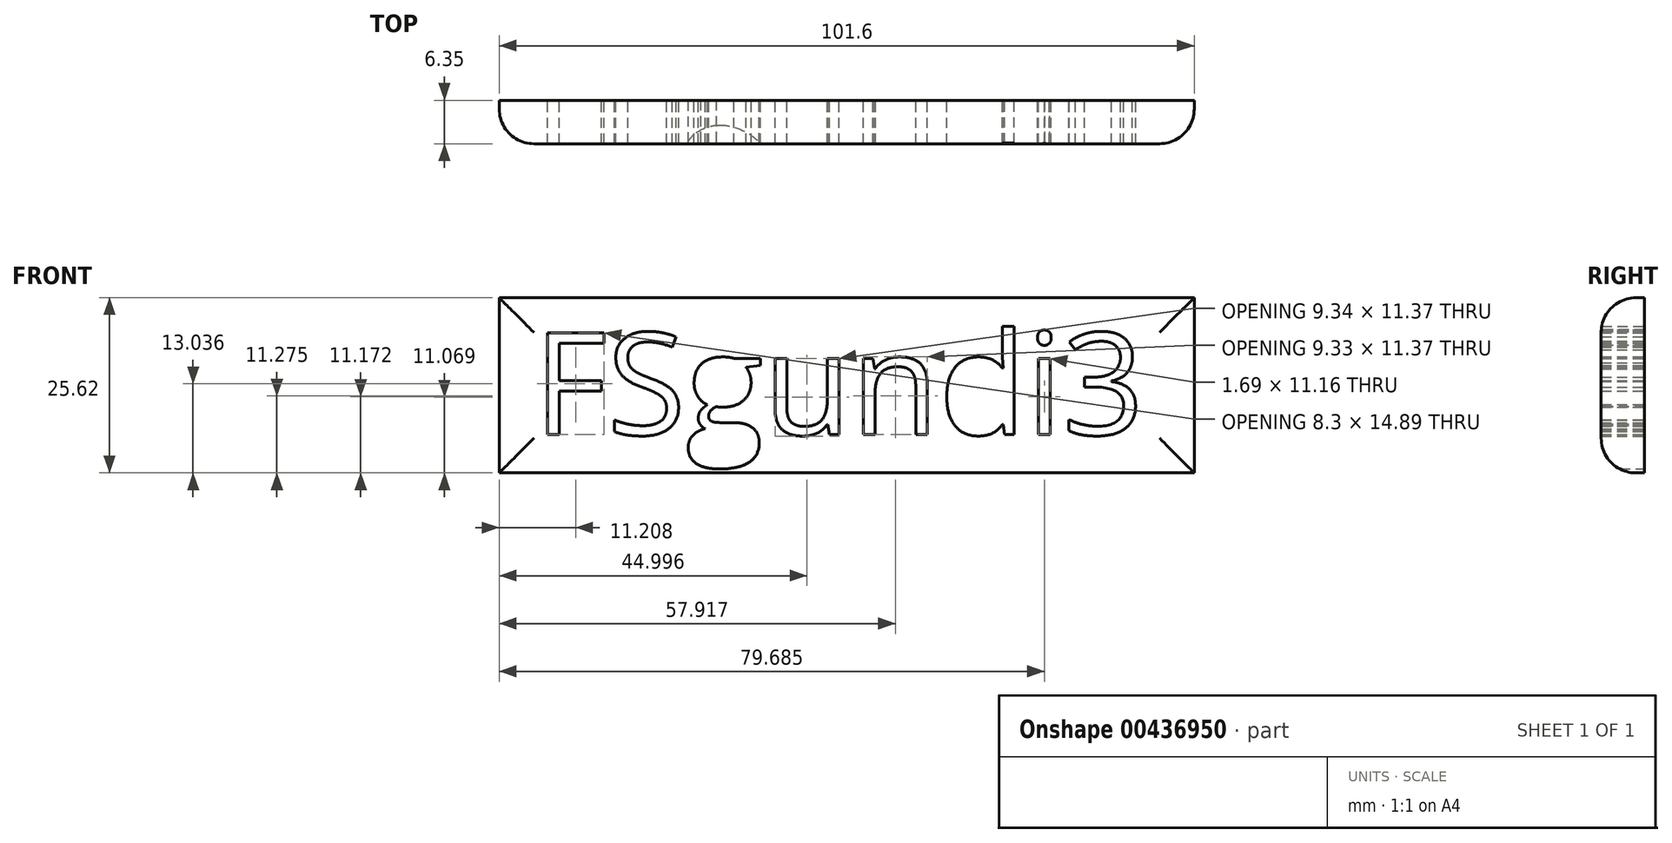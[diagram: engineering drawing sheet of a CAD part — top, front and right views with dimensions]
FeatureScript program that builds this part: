
annotation { "Feature Type Name" : "Feature", "Feature Type Description" : "" }
export const myFeature = defineFeature(function(context is Context, id is Id, definition is map)
    precondition{}
    {
        {
            var Q0;
            Q0=qCreatedBy(makeId("Front.planeOp"),FACE);
            var sketch = newSketch(context, id + "F0", { "sketchPlane" : qUnion([Q0])});
            skText(sketch, "E0", { "text": "FSgundi3", "fontName": "OpenSans-Regular.ttf"});
            skLineSegment(sketch, "E1.bottom", {"start": v(-48.6, 15.35) * mm, "end": v(53, 15.35) * mm});
            skLineSegment(sketch, "E1.top", {"start": v(-48.6, -10.27) * mm, "end": v(53, -10.27) * mm});
            skLineSegment(sketch, "E1.left", {"start": v(-48.6, 15.35) * mm, "end": v(-48.6, -10.27) * mm});
            skLineSegment(sketch, "E1.right", {"start": v(53, 15.35) * mm, "end": v(53, -10.27) * mm});
            const initialGuessF0  = {"E0": [-0.0436, -0.00468, 1, 0, 0.01502]};
            skSetInitialGuess(sketch, initialGuessF0);
            skSolve(sketch);
        }
        {
            var Q0;
            Q0=makeQuery(id+"F0.imprint","IMPRINT",FACE,{"disambiguationData":[TD([[makeQuery(id+"F0.imprint","IMPRINT",EDGE,{"derivedFrom":sQuery(id+"F0.wireOp",EDGE,"E0.sketch_text.stroke-0")}),1.0]])]});
            extrude(context, id + "F1", {"entities" : qUnion([Q0]), "depth" : 6.35 * mm});
        }
        {
            var Q0;
            Q0=makeQuery(id+"F1.opExtrude","CAP_EDGE",EDGE,{"disambiguationData":[OSD([sQuery(id+"F0.wireOp",EDGE,"E1.bottom")])],"isStart":false});
            var Q1;
            Q1=makeQuery(id+"F1.opExtrude","CAP_EDGE",EDGE,{"disambiguationData":[OSD([sQuery(id+"F0.wireOp",EDGE,"E1.top")])],"isStart":false});
            var Q2;
            Q2=makeQuery(id+"F1.opExtrude","CAP_EDGE",EDGE,{"disambiguationData":[OSD([sQuery(id+"F0.wireOp",EDGE,"E1.right")])],"isStart":false});
            var Q3;
            Q3=makeQuery(id+"F1.opExtrude","CAP_EDGE",EDGE,{"disambiguationData":[OSD([sQuery(id+"F0.wireOp",EDGE,"E1.left")])],"isStart":false});
            fillet(context, id + "F2", {"entities" : qUnion([Q0, Q1, Q2, Q3]), "radius" : 5.08 * mm, "tangentPropagation" : true, "allowEdgeOverflow" : false});
        }
    });
